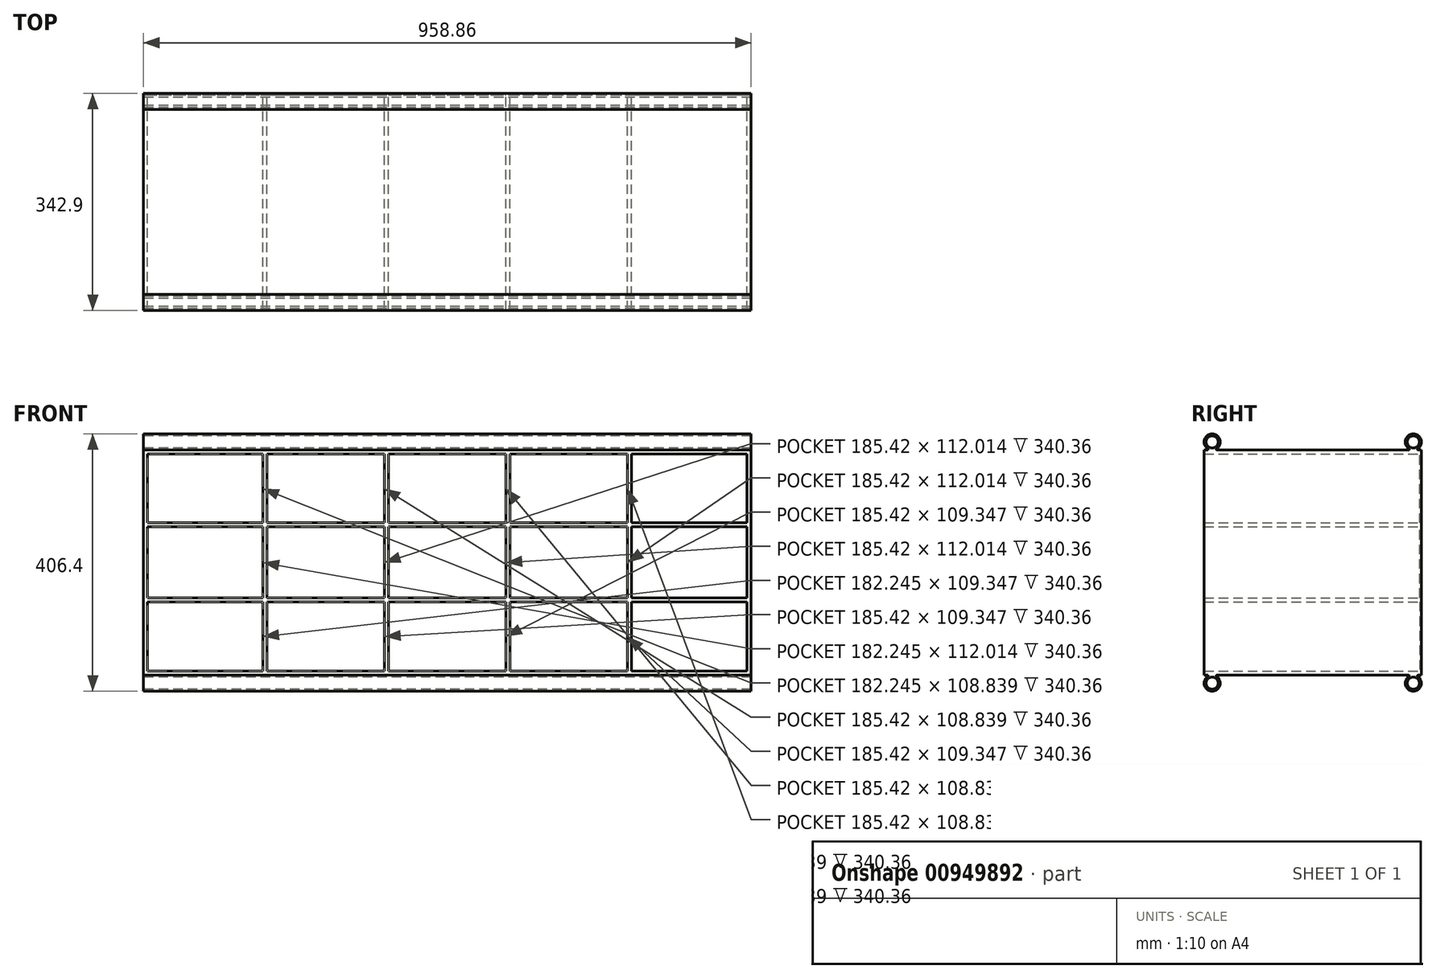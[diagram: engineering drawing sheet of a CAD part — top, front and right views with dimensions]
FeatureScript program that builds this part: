
annotation { "Feature Type Name" : "Feature", "Feature Type Description" : "" }
export const myFeature = defineFeature(function(context is Context, id is Id, definition is map)
    precondition{}
    {
        {
            var Q0;
            Q0=qCreatedBy(makeId("Right.planeOp"),FACE);
            var sketch = newSketch(context, id + "F0", { "sketchPlane" : qUnion([Q0])});
            skLineSegment(sketch, "E0.bottom", {"start": v(0, 0) * mm, "end": v(-342.9, 0) * mm});
            skLineSegment(sketch, "E0.top", {"start": v(0, 355.6) * mm, "end": v(-342.9, 355.6) * mm});
            skLineSegment(sketch, "E0.left", {"start": v(0, 0) * mm, "end": v(0, 355.6) * mm});
            skLineSegment(sketch, "E0.right", {"start": v(-342.9, 0) * mm, "end": v(-342.9, 355.6) * mm});
            skSolve(sketch);
        }
        {
            var Q0;
            Q0=makeQuery(id+"F0.imprint","IMPRINT",FACE,{"disambiguationData":[TD([[makeQuery(id+"F0.imprint","IMPRINT",EDGE,{"derivedFrom":sQuery(id+"F0.wireOp",EDGE,"E0.bottom")}),-1.0]])]});
            extrude(context, id + "F1", {"entities" : qUnion([Q0]), "endBound" : BoundingType.SYMMETRIC, "depth" : 958.85 * mm, "offsetDistance" : 25.4 * mm});
        }
        {
            var Q0;
            Q0=makeQuery(id+"F1.opExtrude","SWEPT_FACE",FACE,{"disambiguationData":[OSD([sQuery(id+"F0.wireOp",EDGE,"E0.right")])]});
            shell(context, id + "F2", {"entities" : qUnion([Q0]), "thickness" : 2.54 * mm});
        }
        {
            var Q0;
            Q0=makeQuery(id+"F1.opExtrude","CAP_FACE",FACE,{"disambiguationData":[OSD([sQuery(id+"F0.wireOp",EDGE,"E0.bottom"),sQuery(id+"F0.wireOp",EDGE,"E0.top"),sQuery(id+"F0.wireOp",EDGE,"E0.left"),sQuery(id+"F0.wireOp",EDGE,"E0.right")])],"isStart":true});
            var sketch = newSketch(context, id + "F3", { "sketchPlane" : qUnion([Q0])});
            skArc(sketch, "E1", {"start": v(19.05, 357.3) * mm, "mid": v(12.7, 381) * mm, "end": v(6.35, 357.3) * mm});
            skArc(sketch, "E2", {"start": v(336.55, 357.3) * mm, "mid": v(330.2, 381) * mm, "end": v(323.85, 357.3) * mm});
            skArc(sketch, "E3", {"start": v(6.35, -1.7) * mm, "mid": v(12.7, -25.4) * mm, "end": v(19.05, -1.7) * mm});
            skArc(sketch, "E4", {"start": v(323.85, -1.7) * mm, "mid": v(330.2, -25.4) * mm, "end": v(336.55, -1.7) * mm});
            skCircle(sketch, "E5", {"center": v(12.7, 368.3) * mm, "radius": 9.53 * mm});
            skCircle(sketch, "E6", {"center": v(330.2, 368.3) * mm, "radius": 9.53 * mm});
            skCircle(sketch, "E7", {"center": v(330.2, -12.7) * mm, "radius": 9.53 * mm});
            skCircle(sketch, "E8", {"center": v(12.7, -12.7) * mm, "radius": 9.53 * mm});
            skLineSegment(sketch, "E9", {"start": v(6.35, 357.3) * mm, "end": v(6.35, 355.6) * mm});
            skLineSegment(sketch, "E10", {"start": v(19.05, 357.3) * mm, "end": v(19.05, 355.6) * mm});
            skLineSegment(sketch, "E11", {"start": v(6.35, 0) * mm, "end": v(6.35, -1.7) * mm});
            skLineSegment(sketch, "E12", {"start": v(19.05, 0) * mm, "end": v(19.05, -1.7) * mm});
            skLineSegment(sketch, "E13", {"start": v(336.55, 357.3) * mm, "end": v(336.55, 355.6) * mm});
            skLineSegment(sketch, "E14", {"start": v(323.85, 357.3) * mm, "end": v(323.85, 355.6) * mm});
            skLineSegment(sketch, "E15", {"start": v(336.55, 0) * mm, "end": v(336.55, -1.7) * mm});
            skLineSegment(sketch, "E16", {"start": v(323.85, 0) * mm, "end": v(323.85, -1.7) * mm});
            skLineSegment(sketch, "E17", {"start": v(323.85, 355.6) * mm, "end": v(336.55, 355.6) * mm});
            skLineSegment(sketch, "E18", {"start": v(6.35, 355.6) * mm, "end": v(19.05, 355.6) * mm});
            skLineSegment(sketch, "E19", {"start": v(6.35, 0) * mm, "end": v(19.05, 0) * mm});
            skLineSegment(sketch, "E20", {"start": v(323.85, 0) * mm, "end": v(336.55, 0) * mm});
            skSolve(sketch);
        }
        {
            var Q0;
            Q0 = qSketchRegion(id + "F3", true);
            var Q1;
            Q1=makeQuery(id+"F1.opExtrude","CAP_FACE",FACE,{"disambiguationData":[OSD([sQuery(id+"F0.wireOp",EDGE,"E0.bottom"),sQuery(id+"F0.wireOp",EDGE,"E0.top"),sQuery(id+"F0.wireOp",EDGE,"E0.left"),sQuery(id+"F0.wireOp",EDGE,"E0.right")])],"isStart":false});
            extrude(context, id + "F4", {"entities" : qUnion([Q0]), "operationType" : NewBodyOperationType.ADD, "endBound" : BoundingType.UP_TO_SURFACE, "oppositeDirection" : true, "depth" : 25.4 * mm, "endBoundEntityFace" : qUnion([Q1]), "offsetDistance" : 25.4 * mm});
        }
        {
            var Q0;
            Q0=makeQuery(id+"F1.opExtrude","SWEPT_FACE",FACE,{"disambiguationData":[OSD([sQuery(id+"F0.wireOp",EDGE,"E0.left")])]});
            var sketch = newSketch(context, id + "F5", { "sketchPlane" : qUnion([Q0])});
            skLineSegment(sketch, "E21", {"start": v(-479.43, 237.24) * mm, "end": v(479.43, 237.24) * mm, "construction": true});
            skLineSegment(sketch, "E22", {"start": v(-479.43, 118.87) * mm, "end": v(479.43, 118.87) * mm, "construction": true});
            skLineSegment(sketch, "E23", {"start": v(-287.66, 355.6) * mm, "end": v(-287.65, 0) * mm, "construction": true});
            skLineSegment(sketch, "E24", {"start": v(-95.88, 355.6) * mm, "end": v(-95.88, 0) * mm, "construction": true});
            skLineSegment(sketch, "E25", {"start": v(95.89, 355.6) * mm, "end": v(95.89, 0) * mm, "construction": true});
            skLineSegment(sketch, "E26", {"start": v(287.66, 355.6) * mm, "end": v(287.66, 0) * mm, "construction": true});
            skLineSegment(sketch, "E27", {"start": v(479.43, 355.6) * mm, "end": v(479.43, 0) * mm});
            skLineSegment(sketch, "E28.bottom", {"start": v(-473.08, 349.25) * mm, "end": v(-290.83, 349.25) * mm});
            skLineSegment(sketch, "E28.top", {"start": v(-473.08, 6.35) * mm, "end": v(-290.83, 6.35) * mm});
            skLineSegment(sketch, "E28.left", {"start": v(-473.08, 349.25) * mm, "end": v(-473.08, 240.41) * mm});
            skLineSegment(sketch, "E28.right", {"start": v(473.08, 349.25) * mm, "end": v(473.08, 240.41) * mm});
            skLineSegment(sketch, "E29", {"start": v(-290.83, 349.25) * mm, "end": v(-290.83, 240.41) * mm});
            skLineSegment(sketch, "E30", {"start": v(-284.48, 6.35) * mm, "end": v(-284.48, 115.7) * mm});
            skLineSegment(sketch, "E31", {"start": v(-99.06, 349.25) * mm, "end": v(-99.06, 240.41) * mm});
            skLineSegment(sketch, "E32", {"start": v(-92.7, 349.25) * mm, "end": v(-92.7, 240.41) * mm});
            skLineSegment(sketch, "E33", {"start": v(92.71, 349.25) * mm, "end": v(92.71, 240.41) * mm});
            skLineSegment(sketch, "E34", {"start": v(99.06, 349.25) * mm, "end": v(99.06, 240.41) * mm});
            skLineSegment(sketch, "E35", {"start": v(284.48, 349.25) * mm, "end": v(284.48, 240.41) * mm});
            skLineSegment(sketch, "E36", {"start": v(290.83, 349.25) * mm, "end": v(290.83, 240.41) * mm});
            skLineSegment(sketch, "E37.trimOffspring", {"start": v(-284.48, 349.25) * mm, "end": v(-99.06, 349.25) * mm});
            skLineSegment(sketch, "E38.trimOffspring", {"start": v(-92.7, 349.25) * mm, "end": v(92.71, 349.25) * mm});
            skLineSegment(sketch, "E39.trimOffspring", {"start": v(290.83, 349.25) * mm, "end": v(473.08, 349.25) * mm});
            skLineSegment(sketch, "E40.trimOffspring", {"start": v(99.06, 349.25) * mm, "end": v(284.48, 349.25) * mm});
            skLineSegment(sketch, "E41.trimOffspring", {"start": v(290.83, 6.35) * mm, "end": v(473.08, 6.35) * mm});
            skLineSegment(sketch, "E42.trimOffspring", {"start": v(99.06, 6.35) * mm, "end": v(284.48, 6.35) * mm});
            skLineSegment(sketch, "E43.trimOffspring", {"start": v(-92.7, 6.35) * mm, "end": v(92.71, 6.35) * mm});
            skLineSegment(sketch, "E44.trimOffspring", {"start": v(-284.48, 6.35) * mm, "end": v(-99.06, 6.35) * mm});
            skLineSegment(sketch, "E45", {"start": v(-473.08, 115.7) * mm, "end": v(-290.83, 115.7) * mm});
            skLineSegment(sketch, "E46", {"start": v(473.08, 122.05) * mm, "end": v(290.83, 122.05) * mm});
            skLineSegment(sketch, "E47", {"start": v(-473.08, 240.41) * mm, "end": v(-290.83, 240.41) * mm});
            skLineSegment(sketch, "E48", {"start": v(473.08, 234.06) * mm, "end": v(290.83, 234.06) * mm});
            skLineSegment(sketch, "E49.trimOffspring", {"start": v(-473.08, 234.06) * mm, "end": v(-473.08, 122.05) * mm});
            skLineSegment(sketch, "E50.trimOffspring", {"start": v(-473.08, 115.7) * mm, "end": v(-473.08, 6.35) * mm});
            skLineSegment(sketch, "E51.trimOffspring", {"start": v(473.08, 234.06) * mm, "end": v(473.08, 122.05) * mm});
            skLineSegment(sketch, "E52.trimOffspring", {"start": v(473.08, 115.7) * mm, "end": v(473.08, 6.35) * mm});
            skLineSegment(sketch, "E53.trimOffspring", {"start": v(-284.48, 240.41) * mm, "end": v(-99.06, 240.41) * mm});
            skLineSegment(sketch, "E54.trimOffspring", {"start": v(-290.83, 234.06) * mm, "end": v(-290.83, 122.05) * mm});
            skLineSegment(sketch, "E55.trimOffspring", {"start": v(-290.83, 234.06) * mm, "end": v(-473.08, 234.06) * mm});
            skLineSegment(sketch, "E56.trimOffspring", {"start": v(-284.48, 240.41) * mm, "end": v(-284.48, 349.25) * mm});
            skLineSegment(sketch, "E57.trimOffspring", {"start": v(-290.83, 122.05) * mm, "end": v(-473.08, 122.05) * mm});
            skLineSegment(sketch, "E58.trimOffspring", {"start": v(-290.83, 115.7) * mm, "end": v(-290.83, 6.35) * mm});
            skLineSegment(sketch, "E59.trimOffspring", {"start": v(-284.48, 122.05) * mm, "end": v(-284.48, 234.06) * mm});
            skLineSegment(sketch, "E60.trimOffspring", {"start": v(-284.48, 115.7) * mm, "end": v(-99.06, 115.7) * mm});
            skLineSegment(sketch, "E61.trimOffspring", {"start": v(-92.7, 240.41) * mm, "end": v(92.71, 240.41) * mm});
            skLineSegment(sketch, "E62.trimOffspring", {"start": v(-99.06, 234.06) * mm, "end": v(-99.06, 122.05) * mm});
            skLineSegment(sketch, "E63.trimOffspring", {"start": v(-92.7, 234.06) * mm, "end": v(-92.7, 122.05) * mm});
            skLineSegment(sketch, "E64.trimOffspring", {"start": v(-99.06, 234.06) * mm, "end": v(-284.48, 234.06) * mm});
            skLineSegment(sketch, "E65.trimOffspring", {"start": v(-92.7, 115.7) * mm, "end": v(-92.7, 6.35) * mm});
            skLineSegment(sketch, "E66.trimOffspring", {"start": v(-99.06, 122.05) * mm, "end": v(-284.48, 122.05) * mm});
            skLineSegment(sketch, "E67.trimOffspring", {"start": v(-99.06, 115.7) * mm, "end": v(-99.06, 6.35) * mm});
            skLineSegment(sketch, "E68.trimOffspring", {"start": v(-92.7, 115.7) * mm, "end": v(92.71, 115.7) * mm});
            skLineSegment(sketch, "E69.trimOffspring", {"start": v(92.71, 122.05) * mm, "end": v(-92.7, 122.05) * mm});
            skLineSegment(sketch, "E70.trimOffspring", {"start": v(99.06, 115.7) * mm, "end": v(99.06, 6.35) * mm});
            skLineSegment(sketch, "E71.trimOffspring", {"start": v(99.06, 115.7) * mm, "end": v(284.48, 115.7) * mm});
            skLineSegment(sketch, "E72.trimOffspring", {"start": v(92.71, 115.7) * mm, "end": v(92.71, 6.35) * mm});
            skLineSegment(sketch, "E73.trimOffspring", {"start": v(99.06, 234.06) * mm, "end": v(99.06, 122.05) * mm});
            skLineSegment(sketch, "E74.trimOffspring", {"start": v(99.06, 240.41) * mm, "end": v(284.48, 240.41) * mm});
            skLineSegment(sketch, "E75.trimOffspring", {"start": v(92.71, 234.06) * mm, "end": v(92.71, 122.05) * mm});
            skLineSegment(sketch, "E76.trimOffspring", {"start": v(92.71, 234.06) * mm, "end": v(-92.7, 234.06) * mm});
            skLineSegment(sketch, "E77.trimOffspring", {"start": v(290.83, 240.41) * mm, "end": v(473.08, 240.41) * mm});
            skLineSegment(sketch, "E78.trimOffspring", {"start": v(290.83, 234.06) * mm, "end": v(290.83, 122.05) * mm});
            skLineSegment(sketch, "E79.trimOffspring", {"start": v(284.48, 234.06) * mm, "end": v(99.06, 234.06) * mm});
            skLineSegment(sketch, "E80.trimOffspring", {"start": v(284.48, 234.06) * mm, "end": v(284.48, 122.05) * mm});
            skLineSegment(sketch, "E81.trimOffspring", {"start": v(287.66, 122.05) * mm, "end": v(99.06, 122.05) * mm});
            skLineSegment(sketch, "E82.trimOffspring", {"start": v(290.83, 115.7) * mm, "end": v(290.83, 6.35) * mm});
            skLineSegment(sketch, "E83.trimOffspring", {"start": v(290.83, 115.7) * mm, "end": v(473.08, 115.7) * mm});
            skLineSegment(sketch, "E84.trimOffspring", {"start": v(284.48, 115.7) * mm, "end": v(284.48, 6.35) * mm});
            skLineSegment(sketch, "E85.bottom", {"start": v(-479.43, 355.6) * mm, "end": v(479.43, 355.6) * mm});
            skLineSegment(sketch, "E85.top", {"start": v(-479.43, 0) * mm, "end": v(479.43, 0) * mm});
            skLineSegment(sketch, "E85.left", {"start": v(-479.43, 355.6) * mm, "end": v(-479.43, 0) * mm});
            skSolve(sketch);
        }
        {
            var Q0;
            Q0 = qSketchRegion(id + "F5", true);
            var Q1;
            Q1=makeQuery(id+"F1.opExtrude","SWEPT_FACE",FACE,{"disambiguationData":[OSD([sQuery(id+"F0.wireOp",EDGE,"E0.right")])]});
            extrude(context, id + "F6", {"entities" : qUnion([Q0]), "operationType" : NewBodyOperationType.ADD, "endBound" : BoundingType.UP_TO_SURFACE, "oppositeDirection" : true, "depth" : 25.4 * mm, "endBoundEntityFace" : qUnion([Q1]), "offsetDistance" : 25.4 * mm});
        }
        {
            var Q0;
            Q0=makeQuery(id+"F4.opExtrude","SWEPT_EDGE",EDGE,{"disambiguationData":[OSD([sQuery(id+"F3.wireOp",EDGE,"E2"),sQuery(id+"F3.wireOp",EDGE,"E13")])]});
            var Q1;
            Q1=makeQuery(id+"F4.opExtrude","SWEPT_EDGE",EDGE,{"disambiguationData":[OSD([sQuery(id+"F0.wireOp",EDGE,"E0.top"),sQuery(id+"F3.wireOp",EDGE,"E13"),sQuery(id+"F3.wireOp",EDGE,"E17")])]});
            var Q2;
            Q2=makeQuery(id+"F4.opExtrude","SWEPT_EDGE",EDGE,{"disambiguationData":[OSD([sQuery(id+"F3.wireOp",EDGE,"E2"),sQuery(id+"F3.wireOp",EDGE,"E14")])]});
            var Q3;
            Q3=makeQuery(id+"F4.opExtrude","SWEPT_EDGE",EDGE,{"disambiguationData":[OSD([sQuery(id+"F0.wireOp",EDGE,"E0.top"),sQuery(id+"F3.wireOp",EDGE,"E14"),sQuery(id+"F3.wireOp",EDGE,"E17")])]});
            var Q4;
            Q4=makeQuery(id+"F4.opExtrude","SWEPT_EDGE",EDGE,{"disambiguationData":[OSD([sQuery(id+"F0.wireOp",EDGE,"E0.top"),sQuery(id+"F3.wireOp",EDGE,"E10"),sQuery(id+"F3.wireOp",EDGE,"E18")])]});
            var Q5;
            Q5=makeQuery(id+"F4.opExtrude","SWEPT_EDGE",EDGE,{"disambiguationData":[OSD([sQuery(id+"F3.wireOp",EDGE,"E1"),sQuery(id+"F3.wireOp",EDGE,"E10")])]});
            var Q6;
            Q6=makeQuery(id+"F4.opExtrude","SWEPT_EDGE",EDGE,{"disambiguationData":[OSD([sQuery(id+"F3.wireOp",EDGE,"E1"),sQuery(id+"F3.wireOp",EDGE,"E9")])]});
            var Q7;
            Q7=makeQuery(id+"F4.opExtrude","SWEPT_EDGE",EDGE,{"disambiguationData":[OSD([sQuery(id+"F0.wireOp",EDGE,"E0.top"),sQuery(id+"F3.wireOp",EDGE,"E9"),sQuery(id+"F3.wireOp",EDGE,"E18")])]});
            var Q8;
            Q8=makeQuery(id+"F4.opExtrude","SWEPT_EDGE",EDGE,{"disambiguationData":[OSD([sQuery(id+"F0.wireOp",EDGE,"E0.bottom"),sQuery(id+"F3.wireOp",EDGE,"E11"),sQuery(id+"F3.wireOp",EDGE,"E19")])]});
            var Q9;
            Q9=makeQuery(id+"F4.opExtrude","SWEPT_EDGE",EDGE,{"disambiguationData":[OSD([sQuery(id+"F3.wireOp",EDGE,"E3"),sQuery(id+"F3.wireOp",EDGE,"E11")])]});
            var Q10;
            Q10=makeQuery(id+"F4.opExtrude","SWEPT_EDGE",EDGE,{"disambiguationData":[OSD([sQuery(id+"F0.wireOp",EDGE,"E0.bottom"),sQuery(id+"F3.wireOp",EDGE,"E12"),sQuery(id+"F3.wireOp",EDGE,"E19")])]});
            var Q11;
            Q11=makeQuery(id+"F4.opExtrude","SWEPT_EDGE",EDGE,{"disambiguationData":[OSD([sQuery(id+"F3.wireOp",EDGE,"E3"),sQuery(id+"F3.wireOp",EDGE,"E12")])]});
            var Q12;
            Q12=makeQuery(id+"F4.opExtrude","SWEPT_EDGE",EDGE,{"disambiguationData":[OSD([sQuery(id+"F3.wireOp",EDGE,"E4"),sQuery(id+"F3.wireOp",EDGE,"E16")])]});
            var Q13;
            Q13=makeQuery(id+"F4.opExtrude","SWEPT_EDGE",EDGE,{"disambiguationData":[OSD([sQuery(id+"F0.wireOp",EDGE,"E0.bottom"),sQuery(id+"F3.wireOp",EDGE,"E16"),sQuery(id+"F3.wireOp",EDGE,"E20")])]});
            var Q14;
            Q14=makeQuery(id+"F4.opExtrude","SWEPT_EDGE",EDGE,{"disambiguationData":[OSD([sQuery(id+"F0.wireOp",EDGE,"E0.bottom"),sQuery(id+"F3.wireOp",EDGE,"E15"),sQuery(id+"F3.wireOp",EDGE,"E20")])]});
            var Q15;
            Q15=makeQuery(id+"F4.opExtrude","SWEPT_EDGE",EDGE,{"disambiguationData":[OSD([sQuery(id+"F3.wireOp",EDGE,"E4"),sQuery(id+"F3.wireOp",EDGE,"E15")])]});
            fillet(context, id + "F7", {"entities" : qUnion([Q0, Q1, Q2, Q3, Q4, Q5, Q6, Q7, Q8, Q9, Q10, Q11, Q12, Q13, Q14, Q15]), "radius" : 1.02 * mm, "tangentPropagation" : true, "allowEdgeOverflow" : false});
        }
    });
